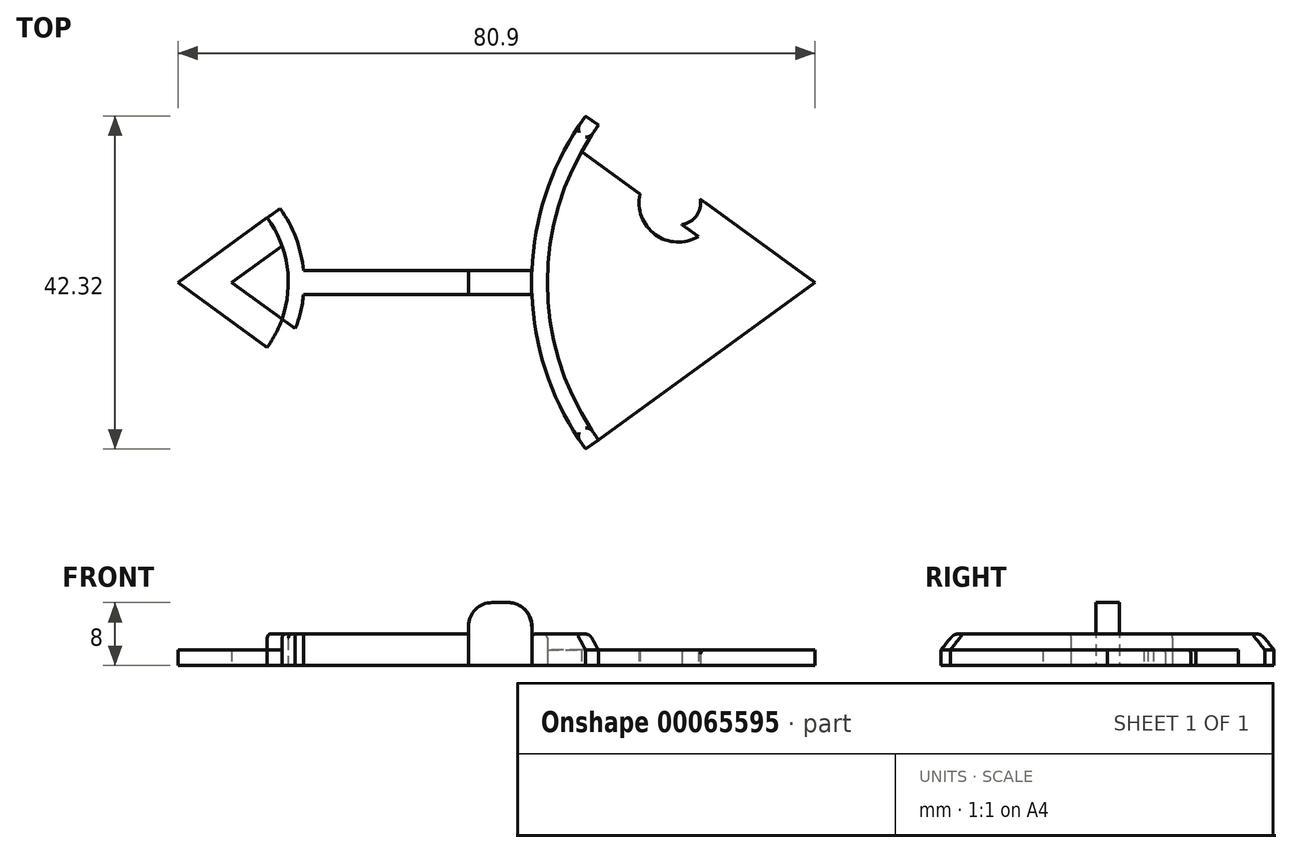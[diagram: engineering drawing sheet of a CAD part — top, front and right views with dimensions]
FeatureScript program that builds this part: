
annotation { "Feature Type Name" : "Feature", "Feature Type Description" : "" }
export const myFeature = defineFeature(function(context is Context, id is Id, definition is map)
    precondition{}
    {
        {
            var Q0;
            Q0=qCreatedBy(makeId("Top.planeOp"),FACE);
            var sketch = newSketch(context, id + "F0", { "sketchPlane" : qUnion([Q0])});
            skPoint(sketch, "E0.MirrorCS.end.orphan", {"position": v(-14.56, -18.8) * mm});
            skPoint(sketch, "E1.MirrorCS.start.orphan", {"position": v(-25.89, -10.58) * mm});
            skLineSegment(sketch, "E2.MirrorCS", {"start": v(40.45, 0) * mm, "end": v(25.89, 10.58) * mm});
            skLineSegment(sketch, "E3.MirrorCS", {"start": v(40.45, 0) * mm, "end": v(0, -29.39) * mm});
            skLineSegment(sketch, "E4.0", {"start": v(-33.65, 0) * mm, "end": v(-25.57, 5.87) * mm});
            skLineSegment(sketch, "E5.trimOffspring", {"start": v(33.65, 0) * mm, "end": v(0, 24.44) * mm});
            skLineSegment(sketch, "E6.trimOffspring", {"start": v(22.65, 12.93) * mm, "end": v(0, 29.39) * mm});
            skArc(sketch, "E7", {"start": v(-27.5, 9.4) * mm, "mid": v(-24.45, 0) * mm, "end": v(-27.5, -9.4) * mm});
            skArc(sketch, "E8", {"start": v(-29.12, -8.23) * mm, "mid": v(-26.45, 0) * mm, "end": v(-29.12, 8.23) * mm});
            skArc(sketch, "E9", {"start": v(12.94, 19.98) * mm, "mid": v(6.45, 0) * mm, "end": v(12.94, -19.98) * mm});
            skArc(sketch, "E10", {"start": v(11.33, -21.16) * mm, "mid": v(4.45, 0) * mm, "end": v(11.33, 21.16) * mm});
            skLineSegment(sketch, "E11", {"start": v(-24.52, 1.5) * mm, "end": v(4.48, 1.5) * mm});
            skLineSegment(sketch, "E12.MirrorCS", {"start": v(-24.52, -1.5) * mm, "end": v(4.48, -1.5) * mm});
            skLineSegment(sketch, "E13", {"start": v(-3.55, 1.5) * mm, "end": v(-3.55, -1.5) * mm});
            skLineSegment(sketch, "E14.MirrorCS", {"start": v(-25.89, -10.58) * mm, "end": v(-29.12, -12.93) * mm});
            skLineSegment(sketch, "E15.MirrorCS", {"start": v(-29.12, -12.93) * mm, "end": v(-27.89, -16.74) * mm});
            skLineSegment(sketch, "E16.MirrorCS", {"start": v(-27.89, -16.74) * mm, "end": v(-23.89, -16.74) * mm});
            skLineSegment(sketch, "E17.MirrorCS", {"start": v(-15.8, -22.61) * mm, "end": v(-14.56, -18.8) * mm});
            skLineSegment(sketch, "E18.MirrorCS", {"start": v(-25.18, 4.78) * mm, "end": v(-19.2, 4.78) * mm});
            skLineSegment(sketch, "E19.MirrorCS", {"start": v(-19.2, 4.78) * mm, "end": v(-16.77, 12.26) * mm});
            skLineSegment(sketch, "E20.trimOffspring", {"start": v(-16.77, 12.26) * mm, "end": v(0, 24.44) * mm});
            skLineSegment(sketch, "E21.trimOffspring", {"start": v(-14.56, -18.8) * mm, "end": v(0, -29.39) * mm});
            skArc(sketch, "E22.MirrorCS", {"start": v(25.89, -10.58) * mm, "mid": v(27.1, -15.66) * mm, "end": v(22.65, -12.93) * mm});
            skArc(sketch, "E23.MirrorCS", {"start": v(25.89, 10.58) * mm, "mid": v(21.43, 7.85) * mm, "end": v(22.65, 12.93) * mm});
            skLineSegment(sketch, "E24.MirrorCS", {"start": v(24.27, 11.76) * mm, "end": v(23.1, 10.14) * mm});
            skArc(sketch, "E25.MirrorCS", {"start": v(25.63, 5.83) * mm, "mid": v(20.16, 6.1) * mm, "end": v(18.21, 11.21) * mm});
            skLineSegment(sketch, "E26", {"start": v(-40.45, 0) * mm, "end": v(0, -29.39) * mm});
            skLineSegment(sketch, "E27", {"start": v(-33.65, 0) * mm, "end": v(0, -24.44) * mm});
            skLineSegment(sketch, "E28", {"start": v(0, -24.44) * mm, "end": v(33.65, 0) * mm});
            skLineSegment(sketch, "E29", {"start": v(-40.45, 0) * mm, "end": v(0, 29.39) * mm});
            skCircle(sketch, "E30.cCircle", {"center": v(-31.18, 26.5) * mm, "radius": 5.12 * mm, "construction": true});
            skLineSegment(sketch, "E30.0", {"start": v(-25.67, 23.38) * mm, "end": v(-32.45, 20.3) * mm});
            skLineSegment(sketch, "E30.1", {"start": v(-32.45, 20.3) * mm, "end": v(-37.47, 25.8) * mm});
            skLineSegment(sketch, "E30.2", {"start": v(-37.47, 25.8) * mm, "end": v(-33.8, 32.27) * mm});
            skLineSegment(sketch, "E30.3", {"start": v(-33.8, 32.27) * mm, "end": v(-26.5, 30.78) * mm});
            skLineSegment(sketch, "E30.4", {"start": v(-26.5, 30.78) * mm, "end": v(-25.67, 23.38) * mm});
            skPoint(sketch, "E30.0.midPoint", {"position": v(-29.06, 21.84) * mm});
            skSolve(sketch);
        }
        {
            var Q0;
            {var subQ6=sQuery(id+"F0.wireOp",EDGE,"344213ac-8071-403f-a3d1-23381589129e0.MirrorCS");var subQ7=sQuery(id+"F0.wireOp",EDGE,"S7KUV9sC-dkK3-GyF4-MVni-NoWh9EwqWeLP");var subQ8=makeQuery(id+"F0.imprint","INTERSECT",VERTEX,{"derivedFrom":[subQ7,subQ6]});Q0=makeQuery(id+"F0.imprint","IMPRINT",FACE,{"disambiguationData":[TD([[makeQuery(id+"F0.imprint","IMPRINT",EDGE,{"disambiguationData":[TD([[subQ8,-1.0]])],"derivedFrom":subQ7}),-1.0]])]});}
            var Q1;
            {var subQ4=sQuery(id+"F0.wireOp",EDGE,"f5c25928-698e-44d5-8ebd-1ef2e6de32d40.MirrorCS");Q1=makeQuery(id+"F0.imprint","IMPRINT",FACE,{"disambiguationData":[TD([[makeQuery(id+"F0.imprint","IMPRINT",EDGE,{"derivedFrom":subQ4}),1.0]])]});}
            var Q2;
            {var subQ11=sQuery(id+"F0.wireOp",EDGE,"E2.MirrorCS");Q2=makeQuery(id+"F0.imprint","IMPRINT",FACE,{"disambiguationData":[TD([[makeQuery(id+"F0.imprint","IMPRINT",EDGE,{"derivedFrom":subQ11}),1.0]])]});}
            var Q3;
            {var subQ12=sQuery(id+"F0.wireOp",EDGE,"1e3cc2f9-6c97-4a5e-b52b-3ecd6ede057e.1");Q3=makeQuery(id+"F0.imprint","IMPRINT",FACE,{"disambiguationData":[TD([[makeQuery(id+"F0.imprint","IMPRINT",EDGE,{"derivedFrom":subQ12}),-1.0]])]});}
            var Q4;
            {var subQ5=sQuery(id+"F0.wireOp",EDGE,"E5.trimOffspring");var subQ6=makeQuery(id+"F0.imprint","INTERSECT",VERTEX,{"disambiguationData":[OD(1.0)],"derivedFrom":[subQ5,sQuery(id+"F0.wireOp",EDGE,"E25.MirrorCS")]});Q4=makeQuery(id+"F0.imprint","IMPRINT",FACE,{"disambiguationData":[TD([[makeQuery(id+"F0.imprint","IMPRINT",EDGE,{"disambiguationData":[TD([[subQ6,1.0]])],"derivedFrom":subQ5}),-1.0]])]});}
            var Q5;
            {var subQ0=sQuery(id+"F0.wireOp",EDGE,"E25.MirrorCS");Q5=makeQuery(id+"F0.imprint","IMPRINT",FACE,{"disambiguationData":[TD([[makeQuery(id+"F0.imprint","IMPRINT",EDGE,{"derivedFrom":subQ0}),-1.0]])]});}
            var Q6;
            {var subQ9=sQuery(id+"F0.wireOp",EDGE,"ede875de-e8ca-4b59-bd6b-6d31fcd64c07.trimOffspring");Q6=makeQuery(id+"F0.imprint","IMPRINT",FACE,{"disambiguationData":[TD([[makeQuery(id+"F0.imprint","IMPRINT",EDGE,{"derivedFrom":subQ9}),-1.0]])]});}
            var Q7;
            {var subQ5=sQuery(id+"F0.wireOp",EDGE,"E4.0");var subQ8=sQuery(id+"F0.wireOp",EDGE,"E27");var subQ10=makeQuery(id+"F0.imprint","INTERSECT",VERTEX,{"derivedFrom":[subQ5,subQ8]});Q7=makeQuery(id+"F0.imprint","IMPRINT",FACE,{"disambiguationData":[TD([[makeQuery(id+"F0.imprint","IMPRINT",EDGE,{"disambiguationData":[TD([[subQ10,-1.0]])],"derivedFrom":subQ5}),1.0]])]});}
            var Q8;
            {var subQ0=sQuery(id+"F0.wireOp",EDGE,"E26");var subQ5=sQuery(id+"F0.wireOp",EDGE,"E3.MirrorCS");var subQ11=makeQuery(id+"F0.imprint","INTERSECT",VERTEX,{"derivedFrom":[subQ5,subQ0]});Q8=makeQuery(id+"F0.imprint","IMPRINT",FACE,{"disambiguationData":[TD([[makeQuery(id+"F0.imprint","IMPRINT",EDGE,{"disambiguationData":[TD([[subQ11,1.0]])],"derivedFrom":subQ5}),-1.0]])]});}
            var Q9;
            {var subQ1=sQuery(id+"F0.wireOp",EDGE,"E14.MirrorCS");Q9=makeQuery(id+"F0.imprint","IMPRINT",FACE,{"disambiguationData":[TD([[makeQuery(id+"F0.imprint","IMPRINT",EDGE,{"derivedFrom":subQ1}),1.0]])]});}
            var Q10;
            {var subQ0=sQuery(id+"F0.wireOp",EDGE,"E22.MirrorCS");Q10=makeQuery(id+"F0.imprint","IMPRINT",FACE,{"disambiguationData":[TD([[makeQuery(id+"F0.imprint","IMPRINT",EDGE,{"derivedFrom":subQ0}),-1.0]])]});}
            extrude(context, id + "F1", {"entities" : qUnion([Q0, Q1, Q2, Q3, Q4, Q5, Q6, Q7, Q8, Q9, Q10]), "depth" : 2 * mm});
        }
        {
            var Q0;
            Q0=makeQuery(id+"F1.opExtrude","CAP_EDGE",EDGE,{"disambiguationData":[OSD([sQuery(id+"F0.wireOp",EDGE,"E23.MirrorCS")])],"isStart":false});
            var Q1;
            Q1=makeQuery(id+"F1.opExtrude","CAP_EDGE",EDGE,{"disambiguationData":[OSD([sQuery(id+"F0.wireOp",EDGE,"59106934-54f1-435c-a875-06c3c03afd720.MirrorCS")])],"isStart":false});
            var Q2;
            Q2=makeQuery(id+"F1.opExtrude","CAP_EDGE",EDGE,{"disambiguationData":[OSD([sQuery(id+"F0.wireOp",EDGE,"678d2bcb-ae43-486a-a37f-476ad2ac9cbf0.MirrorCS")])],"isStart":false});
            var Q3;
            Q3=makeQuery(id+"F1.opExtrude","CAP_EDGE",EDGE,{"disambiguationData":[OSD([sQuery(id+"F0.wireOp",EDGE,"d9e8f044-0c2d-419d-a20d-1ed3d614f8630.MirrorCS")])],"isStart":false});
            var Q4;
            Q4=makeQuery(id+"F1.opExtrude","CAP_EDGE",EDGE,{"disambiguationData":[OSD([sQuery(id+"F0.wireOp",EDGE,"b27c10fb-c10d-4bf1-b058-e80fbe36ff810.MirrorCS")])],"isStart":false});
            fillet(context, id + "F2", {"entities" : qUnion([Q0, Q1, Q2, Q3, Q4]), "radius" : 0.5 * mm, "tangentPropagation" : true, "allowEdgeOverflow" : false});
        }
        {
            var Q0;
            {var subQ0=sQuery(id+"F0.wireOp",EDGE,"E7");var subQ1=sQuery(id+"F0.wireOp",EDGE,"S7KUV9sC-dkK3-GyF4-MVni-NoWh9EwqWeLP");var subQ2=makeQuery(id+"F0.imprint","INTERSECT",VERTEX,{"derivedFrom":[subQ1,subQ0]});Q0=makeQuery(id+"F0.imprint","IMPRINT",FACE,{"disambiguationData":[TD([[makeQuery(id+"F0.imprint","IMPRINT",EDGE,{"disambiguationData":[TD([[subQ2,1.0]])],"derivedFrom":subQ1}),-1.0]])]});}
            var Q1;
            {var subQ1=sQuery(id+"F0.wireOp",EDGE,"E4.0");var subQ7=sQuery(id+"F0.wireOp",EDGE,"E8");var subQ9=makeQuery(id+"F0.imprint","INTERSECT",VERTEX,{"derivedFrom":[subQ1,subQ7]});Q1=makeQuery(id+"F0.imprint","IMPRINT",FACE,{"disambiguationData":[TD([[makeQuery(id+"F0.imprint","IMPRINT",EDGE,{"disambiguationData":[TD([[subQ9,-1.0]])],"derivedFrom":subQ1}),-1.0]])]});}
            var Q2;
            {var subQ0=sQuery(id+"F0.wireOp",EDGE,"E7");var subQ1=sQuery(id+"F0.wireOp",EDGE,"344213ac-8071-403f-a3d1-23381589129e0.MirrorCS");var subQ2=makeQuery(id+"F0.imprint","INTERSECT",VERTEX,{"derivedFrom":[subQ1,subQ0]});Q2=makeQuery(id+"F0.imprint","IMPRINT",FACE,{"disambiguationData":[TD([[makeQuery(id+"F0.imprint","IMPRINT",EDGE,{"disambiguationData":[TD([[subQ2,1.0]])],"derivedFrom":subQ1}),1.0]])]});}
            var Q3;
            {var subQ0=sQuery(id+"F0.wireOp",EDGE,"E9");var subQ1=sQuery(id+"F0.wireOp",EDGE,"E5.trimOffspring");var subQ2=makeQuery(id+"F0.imprint","INTERSECT",VERTEX,{"derivedFrom":[subQ1,subQ0]});Q3=makeQuery(id+"F0.imprint","IMPRINT",FACE,{"disambiguationData":[TD([[makeQuery(id+"F0.imprint","IMPRINT",EDGE,{"disambiguationData":[TD([[subQ2,-1.0]])],"derivedFrom":subQ1}),1.0]])]});}
            var Q4;
            {var subQ0=sQuery(id+"F0.wireOp",EDGE,"E9");var subQ1=sQuery(id+"F0.wireOp",EDGE,"E3.MirrorCS");var subQ2=makeQuery(id+"F0.imprint","INTERSECT",VERTEX,{"derivedFrom":[subQ1,subQ0]});Q4=makeQuery(id+"F0.imprint","IMPRINT",FACE,{"disambiguationData":[TD([[makeQuery(id+"F0.imprint","IMPRINT",EDGE,{"disambiguationData":[TD([[subQ2,-1.0]])],"derivedFrom":subQ1}),-1.0]])]});}
            var Q5;
            {var subQ0=sQuery(id+"F0.wireOp",EDGE,"E9");var subQ1=sQuery(id+"F0.wireOp",EDGE,"E5.trimOffspring");var subQ2=makeQuery(id+"F0.imprint","INTERSECT",VERTEX,{"derivedFrom":[subQ1,subQ0]});Q5=makeQuery(id+"F0.imprint","IMPRINT",FACE,{"disambiguationData":[TD([[makeQuery(id+"F0.imprint","IMPRINT",EDGE,{"disambiguationData":[TD([[subQ2,-1.0]])],"derivedFrom":subQ1}),-1.0]])]});}
            var Q6;
            {var subQ5=sQuery(id+"F0.wireOp",EDGE,"E13");Q6=makeQuery(id+"F0.imprint","IMPRINT",FACE,{"disambiguationData":[TD([[makeQuery(id+"F0.imprint","IMPRINT",EDGE,{"derivedFrom":subQ5}),-1.0]])]});}
            var Q7;
            {var subQ0=sQuery(id+"F0.wireOp",EDGE,"E26");var subQ1=sQuery(id+"F0.wireOp",EDGE,"E7");var subQ2=makeQuery(id+"F0.imprint","INTERSECT",VERTEX,{"derivedFrom":[subQ1,subQ0]});Q7=makeQuery(id+"F0.imprint","IMPRINT",FACE,{"disambiguationData":[TD([[makeQuery(id+"F0.imprint","IMPRINT",EDGE,{"disambiguationData":[TD([[subQ2,1.0]])],"derivedFrom":subQ1}),-1.0]])]});}
            var Q8;
            {var subQ0=sQuery(id+"F0.wireOp",EDGE,"E7");var subQ1=sQuery(id+"F0.wireOp",EDGE,"E4.0");var subQ2=makeQuery(id+"F0.imprint","INTERSECT",VERTEX,{"derivedFrom":[subQ1,subQ0]});Q8=makeQuery(id+"F0.imprint","IMPRINT",FACE,{"disambiguationData":[TD([[makeQuery(id+"F0.imprint","IMPRINT",EDGE,{"disambiguationData":[TD([[subQ2,1.0]])],"derivedFrom":subQ1}),1.0]])]});}
            extrude(context, id + "F3", {"entities" : qUnion([Q0, Q1, Q2, Q3, Q4, Q5, Q6, Q7, Q8]), "depth" : 4 * mm});
        }
        {
            var Q0;
            Q0=makeQuery(id+"F3.opExtrude","CAP_EDGE",EDGE,{"disambiguationData":[OSD([sQuery(id+"F0.wireOp",EDGE,"S7KUV9sC-dkK3-GyF4-MVni-NoWh9EwqWeLP")])],"isStart":false});
            var Q1;
            Q1=makeQuery(id+"F3.opExtrude","CAP_EDGE",EDGE,{"disambiguationData":[OSD([sQuery(id+"F0.wireOp",EDGE,"344213ac-8071-403f-a3d1-23381589129e0.MirrorCS")])],"isStart":false});
            var Q2;
            Q2=makeQuery(id+"F3.opExtrude","CAP_EDGE",EDGE,{"disambiguationData":[OSD([sQuery(id+"F0.wireOp",EDGE,"E6.trimOffspring")])],"isStart":false});
            var Q3;
            Q3=makeQuery(id+"F3.opExtrude","CAP_EDGE",EDGE,{"disambiguationData":[OSD([sQuery(id+"F0.wireOp",EDGE,"E3.MirrorCS")])],"isStart":false});
            chamfer(context, id + "F4", {"entities" : qUnion([Q0, Q1, Q2, Q3]), "width" : 2 * mm, "tangentPropagation" : true});
        }
        {
            var Q0;
            Q0=makeQuery(id+"F3.opExtrude","CAP_EDGE",EDGE,{"disambiguationData":[OSD([sQuery(id+"F0.wireOp",EDGE,"E8")])],"isStart":false});
            var Q1;
            {var subQ0=sQuery(id+"F0.wireOp",EDGE,"S7KUV9sC-dkK3-GyF4-MVni-NoWh9EwqWeLP");Q1=makeQuery(id+"F4.opChamfer","BLEND_EDGE",EDGE,{"blendedFrom":[makeQuery(id+"F3.opExtrude","CAP_EDGE",EDGE,{"disambiguationData":[OSD([subQ0])],"isStart":false}),makeQuery(id+"F3.opExtrude","CAP_FACE",FACE,{"disambiguationData":[OSD([subQ0,sQuery(id+"F0.wireOp",EDGE,"344213ac-8071-403f-a3d1-23381589129e0.MirrorCS"),sQuery(id+"F0.wireOp",EDGE,"E7"),sQuery(id+"F0.wireOp",EDGE,"E8")])],"isStart":false})],"blendedInto":[makeQuery(id+"F3.opExtrude","CAP_FACE",FACE,{"disambiguationData":[OSD([subQ0,sQuery(id+"F0.wireOp",EDGE,"344213ac-8071-403f-a3d1-23381589129e0.MirrorCS"),sQuery(id+"F0.wireOp",EDGE,"E7"),sQuery(id+"F0.wireOp",EDGE,"E8")])],"isStart":false})]});}
            var Q2;
            {var subQ0=sQuery(id+"F0.wireOp",EDGE,"344213ac-8071-403f-a3d1-23381589129e0.MirrorCS");Q2=makeQuery(id+"F4.opChamfer","BLEND_EDGE",EDGE,{"blendedFrom":[makeQuery(id+"F3.opExtrude","CAP_EDGE",EDGE,{"disambiguationData":[OSD([subQ0])],"isStart":false}),makeQuery(id+"F3.opExtrude","CAP_FACE",FACE,{"disambiguationData":[OSD([sQuery(id+"F0.wireOp",EDGE,"S7KUV9sC-dkK3-GyF4-MVni-NoWh9EwqWeLP"),subQ0,sQuery(id+"F0.wireOp",EDGE,"E7"),sQuery(id+"F0.wireOp",EDGE,"E8")])],"isStart":false})],"blendedInto":[makeQuery(id+"F3.opExtrude","CAP_FACE",FACE,{"disambiguationData":[OSD([sQuery(id+"F0.wireOp",EDGE,"S7KUV9sC-dkK3-GyF4-MVni-NoWh9EwqWeLP"),subQ0,sQuery(id+"F0.wireOp",EDGE,"E7"),sQuery(id+"F0.wireOp",EDGE,"E8")])],"isStart":false})]});}
            var Q3;
            {var subQ0=sQuery(id+"F0.wireOp",EDGE,"E6.trimOffspring");Q3=makeQuery(id+"F4.opChamfer","BLEND_EDGE",EDGE,{"blendedFrom":[makeQuery(id+"F3.opExtrude","CAP_EDGE",EDGE,{"disambiguationData":[OSD([subQ0])],"isStart":false}),makeQuery(id+"F3.opExtrude","CAP_FACE",FACE,{"disambiguationData":[OSD([sQuery(id+"F0.wireOp",EDGE,"E3.MirrorCS"),subQ0,sQuery(id+"F0.wireOp",EDGE,"E9"),sQuery(id+"F0.wireOp",EDGE,"E10")])],"isStart":false})],"blendedInto":[makeQuery(id+"F3.opExtrude","CAP_FACE",FACE,{"disambiguationData":[OSD([sQuery(id+"F0.wireOp",EDGE,"E3.MirrorCS"),subQ0,sQuery(id+"F0.wireOp",EDGE,"E9"),sQuery(id+"F0.wireOp",EDGE,"E10")])],"isStart":false})]});}
            var Q4;
            Q4=makeQuery(id+"F3.opExtrude","CAP_EDGE",EDGE,{"disambiguationData":[OSD([sQuery(id+"F0.wireOp",EDGE,"E10")])],"isStart":false});
            var Q5;
            Q5=makeQuery(id+"F3.opExtrude","CAP_EDGE",EDGE,{"disambiguationData":[OSD([sQuery(id+"F0.wireOp",EDGE,"E9")])],"isStart":false});
            var Q6;
            {var subQ0=sQuery(id+"F0.wireOp",EDGE,"E3.MirrorCS");Q6=makeQuery(id+"F4.opChamfer","BLEND_EDGE",EDGE,{"blendedFrom":[makeQuery(id+"F3.opExtrude","CAP_EDGE",EDGE,{"disambiguationData":[OSD([subQ0])],"isStart":false}),makeQuery(id+"F3.opExtrude","CAP_FACE",FACE,{"disambiguationData":[OSD([subQ0,sQuery(id+"F0.wireOp",EDGE,"E6.trimOffspring"),sQuery(id+"F0.wireOp",EDGE,"E9"),sQuery(id+"F0.wireOp",EDGE,"E10")])],"isStart":false})],"blendedInto":[makeQuery(id+"F3.opExtrude","CAP_FACE",FACE,{"disambiguationData":[OSD([subQ0,sQuery(id+"F0.wireOp",EDGE,"E6.trimOffspring"),sQuery(id+"F0.wireOp",EDGE,"E9"),sQuery(id+"F0.wireOp",EDGE,"E10")])],"isStart":false})]});}
            fillet(context, id + "F5", {"entities" : qUnion([Q0, Q1, Q2, Q3, Q4, Q5, Q6]), "radius" : 0.5 * mm, "tangentPropagation" : true, "allowEdgeOverflow" : false});
        }
        {
            var Q0;
            {var subQ5=sQuery(id+"F0.wireOp",EDGE,"E13");Q0=makeQuery(id+"F0.imprint","IMPRINT",FACE,{"disambiguationData":[TD([[makeQuery(id+"F0.imprint","IMPRINT",EDGE,{"derivedFrom":subQ5}),1.0]])]});}
            extrude(context, id + "F6", {"entities" : qUnion([Q0]), "depth" : 8 * mm});
        }
        {
            var Q0;
            Q0=makeQuery(id+"F6.opExtrude","CAP_EDGE",EDGE,{"disambiguationData":[OSD([sQuery(id+"F0.wireOp",EDGE,"E10")])],"isStart":false});
            var Q1;
            Q1=makeQuery(id+"F6.opExtrude","CAP_EDGE",EDGE,{"disambiguationData":[OSD([sQuery(id+"F0.wireOp",EDGE,"E13")])],"isStart":false});
            fillet(context, id + "F7", {"entities" : qUnion([Q0, Q1]), "radius" : 3 * mm, "tangentPropagation" : true, "allowEdgeOverflow" : false});
        }
    });
